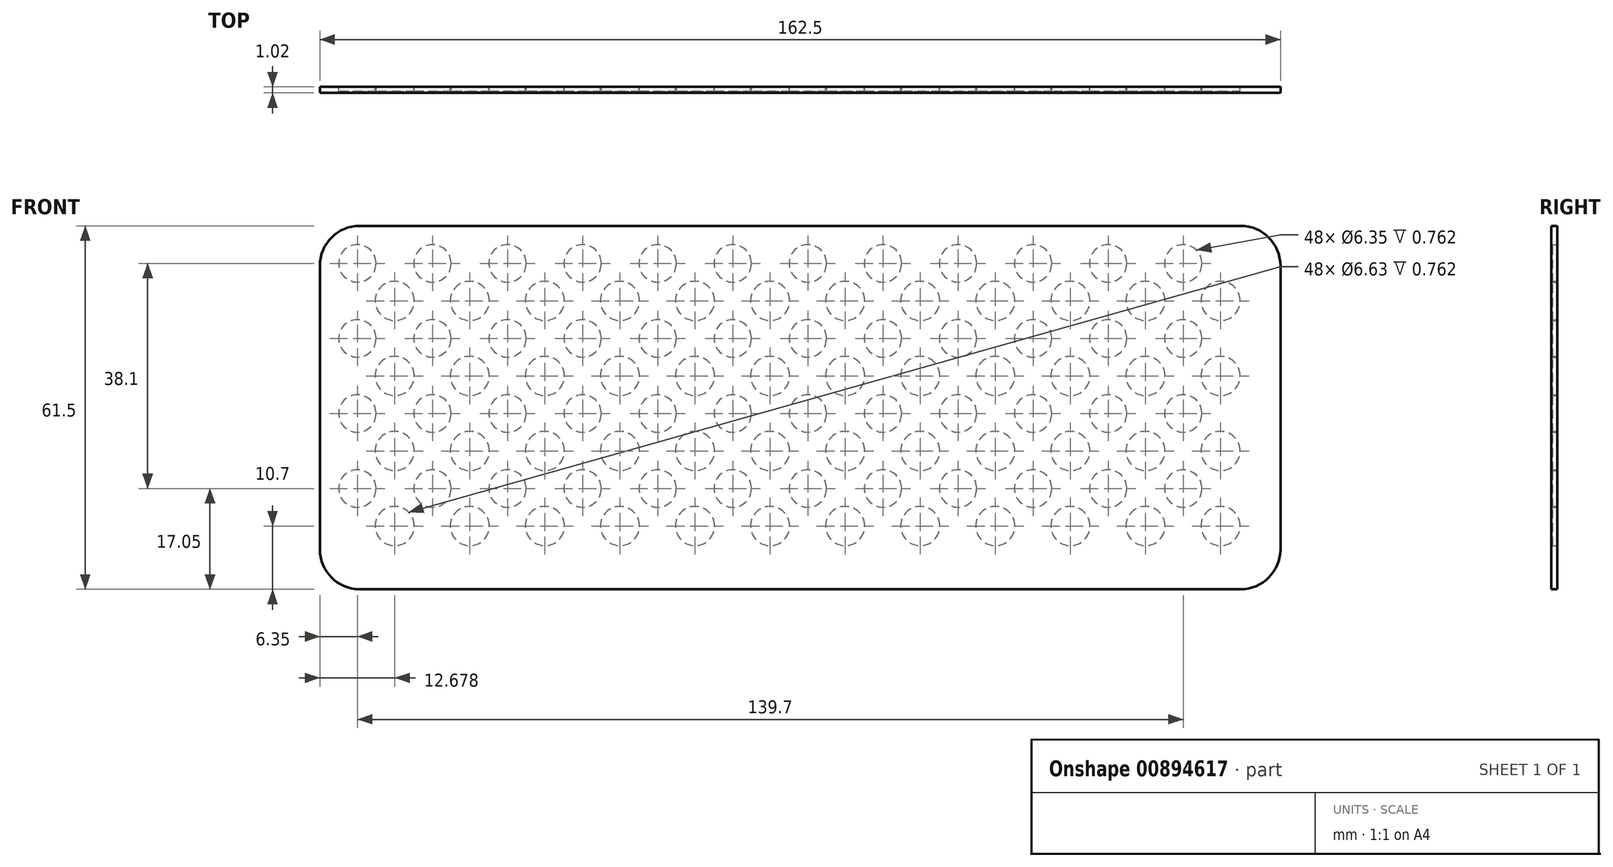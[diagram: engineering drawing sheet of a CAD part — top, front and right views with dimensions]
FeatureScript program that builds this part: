
annotation { "Feature Type Name" : "Feature", "Feature Type Description" : "" }
export const myFeature = defineFeature(function(context is Context, id is Id, definition is map)
    precondition{}
    {
        {
            var Q0;
            Q0=qCreatedBy(makeId("Front.planeOp"),FACE);
            var sketch = newSketch(context, id + "F0", { "sketchPlane" : qUnion([Q0])});
            skLineSegment(sketch, "E0.bottom", {"start": v(74.49, 30.75) * mm, "end": v(-74.49, 30.75) * mm});
            skLineSegment(sketch, "E0.top", {"start": v(74.49, -30.75) * mm, "end": v(-74.49, -30.75) * mm});
            skLineSegment(sketch, "E0.left", {"start": v(81.25, 24) * mm, "end": v(81.25, -23.99) * mm});
            skLineSegment(sketch, "E0.right", {"start": v(-81.25, 24) * mm, "end": v(-81.25, -24) * mm});
            skPoint(sketch, "E0.middle", {"position": v(0, 0) * mm});
            skPoint(sketch, "E1.visualSharp", {"position": v(-81.25, 30.75) * mm});
            skArc(sketch, "E1.filletArc", {"start": v(-74.49, 30.75) * mm, "mid": v(-79.27, 28.77) * mm, "end": v(-81.25, 24) * mm});
            skPoint(sketch, "E2.visualSharp", {"position": v(81.25, 30.75) * mm});
            skArc(sketch, "E2.filletArc", {"start": v(81.25, 24) * mm, "mid": v(79.27, 28.77) * mm, "end": v(74.49, 30.75) * mm});
            skPoint(sketch, "E3.visualSharp", {"position": v(81.25, -30.75) * mm});
            skArc(sketch, "E3.filletArc", {"start": v(74.49, -30.75) * mm, "mid": v(79.27, -28.77) * mm, "end": v(81.25, -24) * mm});
            skPoint(sketch, "E4.visualSharp", {"position": v(-81.25, -30.75) * mm});
            skArc(sketch, "E4.filletArc", {"start": v(-81.25, -24) * mm, "mid": v(-79.27, -28.77) * mm, "end": v(-74.49, -30.75) * mm});
            skSolve(sketch);
        }
        {
            var Q0;
            Q0 = qSketchRegion(id + "F0", true);
            extrude(context, id + "F1", {"entities" : qUnion([Q0]), "depth" : 1.02 * mm, "offsetDistance" : 25.4 * mm});
        }
        {
            var Q0;
            Q0=makeQuery(id+"F0.imprint","IMPRINT",FACE,{"disambiguationData":[TD([[makeQuery(id+"F0.imprint","IMPRINT",EDGE,{"derivedFrom":sQuery(id+"F0.wireOp",EDGE,"E0.bottom")}),1.0]])]});
            var sketch = newSketch(context, id + "F2", { "sketchPlane" : qUnion([Q0])});
            skCircle(sketch, "E5", {"center": v(-74.9, 24.4) * mm, "radius": 3.17 * mm});
            skLineSegment(sketch, "E6.direction1", {"start": v(-74.9, 24.4) * mm, "end": v(-62.2, 24.4) * mm, "construction": true});
            skLineSegment(sketch, "E6.direction2", {"start": v(-74.9, 24.4) * mm, "end": v(-74.94, 11.7) * mm, "construction": true});
            skCircle(sketch, "E7", {"center": v(-68.57, 18.05) * mm, "radius": 3.32 * mm});
            skCircle(sketch, "E8.0.1.0", {"center": v(-68.57, 5.35) * mm, "radius": 3.32 * mm});
            skCircle(sketch, "E8.0.1.1", {"center": v(-74.9, 11.7) * mm, "radius": 3.17 * mm});
            skCircle(sketch, "E8.1.0.0", {"center": v(-55.87, 18.05) * mm, "radius": 3.32 * mm});
            skCircle(sketch, "E8.1.0.1", {"center": v(-62.2, 24.4) * mm, "radius": 3.17 * mm});
            skCircle(sketch, "E8.1.1.0", {"center": v(-55.87, 5.35) * mm, "radius": 3.32 * mm});
            skCircle(sketch, "E8.1.1.1", {"center": v(-62.2, 11.7) * mm, "radius": 3.17 * mm});
            skCircle(sketch, "E8.2.0.0", {"center": v(-43.17, 18.05) * mm, "radius": 3.32 * mm});
            skCircle(sketch, "E8.2.0.1", {"center": v(-49.5, 24.4) * mm, "radius": 3.17 * mm});
            skCircle(sketch, "E8.2.1.0", {"center": v(-43.17, 5.35) * mm, "radius": 3.32 * mm});
            skCircle(sketch, "E8.2.1.1", {"center": v(-49.5, 11.7) * mm, "radius": 3.17 * mm});
            skLineSegment(sketch, "E8.direction1", {"start": v(-68.57, 18.05) * mm, "end": v(-55.87, 18.05) * mm, "construction": true});
            skLineSegment(sketch, "E8.direction2", {"start": v(-68.57, 18.05) * mm, "end": v(-68.57, 5.35) * mm, "construction": true});
            skCircle(sketch, "E9.0.0.2", {"center": v(-68.57, -7.35) * mm, "radius": 3.32 * mm});
            skCircle(sketch, "E9.2.0.2", {"center": v(-74.9, -1) * mm, "radius": 3.17 * mm});
            skCircle(sketch, "E9.0.1.2", {"center": v(-55.87, -7.35) * mm, "radius": 3.32 * mm});
            skCircle(sketch, "E9.2.1.2", {"center": v(-62.2, -1) * mm, "radius": 3.17 * mm});
            skCircle(sketch, "E9.0.2.2", {"center": v(-43.17, -7.35) * mm, "radius": 3.32 * mm});
            skCircle(sketch, "E9.2.2.2", {"center": v(-49.5, -1) * mm, "radius": 3.17 * mm});
            skCircle(sketch, "E10.0.0.3", {"center": v(-68.57, -20.05) * mm, "radius": 3.32 * mm});
            skCircle(sketch, "E10.2.0.3", {"center": v(-74.9, -13.7) * mm, "radius": 3.17 * mm});
            skCircle(sketch, "E10.0.1.3", {"center": v(-55.87, -20.05) * mm, "radius": 3.32 * mm});
            skCircle(sketch, "E10.2.1.3", {"center": v(-62.2, -13.7) * mm, "radius": 3.17 * mm});
            skCircle(sketch, "E10.0.2.3", {"center": v(-43.17, -20.05) * mm, "radius": 3.32 * mm});
            skCircle(sketch, "E10.2.2.3", {"center": v(-49.5, -13.7) * mm, "radius": 3.17 * mm});
            skCircle(sketch, "E11.0.3.0", {"center": v(-30.47, 18.05) * mm, "radius": 3.32 * mm});
            skCircle(sketch, "E11.2.3.0", {"center": v(-36.8, 24.4) * mm, "radius": 3.17 * mm});
            skCircle(sketch, "E11.0.3.1", {"center": v(-30.47, 5.35) * mm, "radius": 3.32 * mm});
            skCircle(sketch, "E11.2.3.1", {"center": v(-36.8, 11.7) * mm, "radius": 3.17 * mm});
            skCircle(sketch, "E11.0.3.2", {"center": v(-30.47, -7.35) * mm, "radius": 3.32 * mm});
            skCircle(sketch, "E11.2.3.2", {"center": v(-36.8, -1) * mm, "radius": 3.17 * mm});
            skCircle(sketch, "E11.0.3.3", {"center": v(-30.47, -20.05) * mm, "radius": 3.32 * mm});
            skCircle(sketch, "E11.2.3.3", {"center": v(-36.8, -13.7) * mm, "radius": 3.17 * mm});
            skCircle(sketch, "E11.0.4.0", {"center": v(-17.77, 18.05) * mm, "radius": 3.32 * mm});
            skCircle(sketch, "E11.2.4.0", {"center": v(-24.1, 24.4) * mm, "radius": 3.17 * mm});
            skCircle(sketch, "E11.0.4.1", {"center": v(-17.77, 5.35) * mm, "radius": 3.32 * mm});
            skCircle(sketch, "E11.2.4.1", {"center": v(-24.1, 11.7) * mm, "radius": 3.17 * mm});
            skCircle(sketch, "E11.0.4.2", {"center": v(-17.77, -7.35) * mm, "radius": 3.32 * mm});
            skCircle(sketch, "E11.2.4.2", {"center": v(-24.1, -1) * mm, "radius": 3.17 * mm});
            skCircle(sketch, "E11.0.4.3", {"center": v(-17.77, -20.05) * mm, "radius": 3.32 * mm});
            skCircle(sketch, "E11.2.4.3", {"center": v(-24.1, -13.7) * mm, "radius": 3.17 * mm});
            skCircle(sketch, "E11.0.5.0", {"center": v(-5.07, 18.05) * mm, "radius": 3.32 * mm});
            skCircle(sketch, "E11.2.5.0", {"center": v(-11.4, 24.4) * mm, "radius": 3.17 * mm});
            skCircle(sketch, "E11.0.5.1", {"center": v(-5.07, 5.35) * mm, "radius": 3.32 * mm});
            skCircle(sketch, "E11.2.5.1", {"center": v(-11.4, 11.7) * mm, "radius": 3.17 * mm});
            skCircle(sketch, "E11.0.5.2", {"center": v(-5.07, -7.35) * mm, "radius": 3.32 * mm});
            skCircle(sketch, "E11.2.5.2", {"center": v(-11.4, -1) * mm, "radius": 3.17 * mm});
            skCircle(sketch, "E11.0.5.3", {"center": v(-5.07, -20.05) * mm, "radius": 3.32 * mm});
            skCircle(sketch, "E11.2.5.3", {"center": v(-11.4, -13.7) * mm, "radius": 3.17 * mm});
            skCircle(sketch, "E11.0.6.0", {"center": v(7.63, 18.05) * mm, "radius": 3.32 * mm});
            skCircle(sketch, "E11.2.6.0", {"center": v(1.3, 24.4) * mm, "radius": 3.17 * mm});
            skCircle(sketch, "E11.0.6.1", {"center": v(7.63, 5.35) * mm, "radius": 3.32 * mm});
            skCircle(sketch, "E11.2.6.1", {"center": v(1.3, 11.7) * mm, "radius": 3.17 * mm});
            skCircle(sketch, "E11.0.6.2", {"center": v(7.63, -7.35) * mm, "radius": 3.32 * mm});
            skCircle(sketch, "E11.2.6.2", {"center": v(1.3, -1) * mm, "radius": 3.17 * mm});
            skCircle(sketch, "E11.0.6.3", {"center": v(7.63, -20.05) * mm, "radius": 3.32 * mm});
            skCircle(sketch, "E11.2.6.3", {"center": v(1.3, -13.7) * mm, "radius": 3.17 * mm});
            skCircle(sketch, "E11.0.7.0", {"center": v(20.33, 18.05) * mm, "radius": 3.32 * mm});
            skCircle(sketch, "E11.2.7.0", {"center": v(14, 24.4) * mm, "radius": 3.17 * mm});
            skCircle(sketch, "E11.0.7.1", {"center": v(20.33, 5.35) * mm, "radius": 3.32 * mm});
            skCircle(sketch, "E11.2.7.1", {"center": v(14, 11.7) * mm, "radius": 3.17 * mm});
            skCircle(sketch, "E11.0.7.2", {"center": v(20.33, -7.35) * mm, "radius": 3.32 * mm});
            skCircle(sketch, "E11.2.7.2", {"center": v(14, -1) * mm, "radius": 3.17 * mm});
            skCircle(sketch, "E11.0.7.3", {"center": v(20.33, -20.05) * mm, "radius": 3.32 * mm});
            skCircle(sketch, "E11.2.7.3", {"center": v(14, -13.7) * mm, "radius": 3.17 * mm});
            skCircle(sketch, "E11.0.8.0", {"center": v(33.03, 18.05) * mm, "radius": 3.32 * mm});
            skCircle(sketch, "E11.2.8.0", {"center": v(26.7, 24.4) * mm, "radius": 3.17 * mm});
            skCircle(sketch, "E11.0.8.1", {"center": v(33.03, 5.35) * mm, "radius": 3.32 * mm});
            skCircle(sketch, "E11.2.8.1", {"center": v(26.7, 11.7) * mm, "radius": 3.17 * mm});
            skCircle(sketch, "E11.0.8.2", {"center": v(33.03, -7.35) * mm, "radius": 3.32 * mm});
            skCircle(sketch, "E11.2.8.2", {"center": v(26.7, -1) * mm, "radius": 3.17 * mm});
            skCircle(sketch, "E11.0.8.3", {"center": v(33.03, -20.05) * mm, "radius": 3.32 * mm});
            skCircle(sketch, "E11.2.8.3", {"center": v(26.7, -13.7) * mm, "radius": 3.17 * mm});
            skCircle(sketch, "E11.0.9.0", {"center": v(45.73, 18.05) * mm, "radius": 3.32 * mm});
            skCircle(sketch, "E11.2.9.0", {"center": v(39.4, 24.4) * mm, "radius": 3.17 * mm});
            skCircle(sketch, "E11.0.9.1", {"center": v(45.73, 5.35) * mm, "radius": 3.32 * mm});
            skCircle(sketch, "E11.2.9.1", {"center": v(39.4, 11.7) * mm, "radius": 3.17 * mm});
            skCircle(sketch, "E11.0.9.2", {"center": v(45.73, -7.35) * mm, "radius": 3.32 * mm});
            skCircle(sketch, "E11.2.9.2", {"center": v(39.4, -1) * mm, "radius": 3.17 * mm});
            skCircle(sketch, "E11.0.9.3", {"center": v(45.73, -20.05) * mm, "radius": 3.32 * mm});
            skCircle(sketch, "E11.2.9.3", {"center": v(39.4, -13.7) * mm, "radius": 3.17 * mm});
            skCircle(sketch, "E12.0.10.0", {"center": v(58.43, 18.05) * mm, "radius": 3.32 * mm});
            skCircle(sketch, "E12.2.10.0", {"center": v(52.1, 24.4) * mm, "radius": 3.17 * mm});
            skCircle(sketch, "E12.0.10.1", {"center": v(58.43, 5.35) * mm, "radius": 3.32 * mm});
            skCircle(sketch, "E12.2.10.1", {"center": v(52.1, 11.7) * mm, "radius": 3.17 * mm});
            skCircle(sketch, "E12.0.10.2", {"center": v(58.43, -7.35) * mm, "radius": 3.32 * mm});
            skCircle(sketch, "E12.2.10.2", {"center": v(52.1, -1) * mm, "radius": 3.17 * mm});
            skCircle(sketch, "E12.0.10.3", {"center": v(58.43, -20.05) * mm, "radius": 3.32 * mm});
            skCircle(sketch, "E12.2.10.3", {"center": v(52.1, -13.7) * mm, "radius": 3.17 * mm});
            skCircle(sketch, "E12.0.11.0", {"center": v(71.13, 18.05) * mm, "radius": 3.32 * mm});
            skCircle(sketch, "E12.2.11.0", {"center": v(64.8, 24.4) * mm, "radius": 3.17 * mm});
            skCircle(sketch, "E12.0.11.1", {"center": v(71.13, 5.35) * mm, "radius": 3.32 * mm});
            skCircle(sketch, "E12.2.11.1", {"center": v(64.8, 11.7) * mm, "radius": 3.17 * mm});
            skCircle(sketch, "E12.0.11.2", {"center": v(71.13, -7.35) * mm, "radius": 3.32 * mm});
            skCircle(sketch, "E12.2.11.2", {"center": v(64.8, -1) * mm, "radius": 3.17 * mm});
            skCircle(sketch, "E12.0.11.3", {"center": v(71.13, -20.05) * mm, "radius": 3.32 * mm});
            skCircle(sketch, "E12.2.11.3", {"center": v(64.8, -13.7) * mm, "radius": 3.17 * mm});
            skLineSegment(sketch, "E13", {"start": v(-68.57, 18.05) * mm, "end": v(-74.9, 18.07) * mm});
            skLineSegment(sketch, "E14", {"start": v(-68.57, 24.4) * mm, "end": v(-68.57, 18.05) * mm});
            skSolve(sketch);
        }
        {
            var Q0;
            Q0 = qSketchRegion(id + "F2", true);
            extrude(context, id + "F3", {"entities" : qUnion([Q0]), "operationType" : NewBodyOperationType.REMOVE, "depth" : 0.76 * mm, "offsetDistance" : 25.4 * mm});
        }
    });
